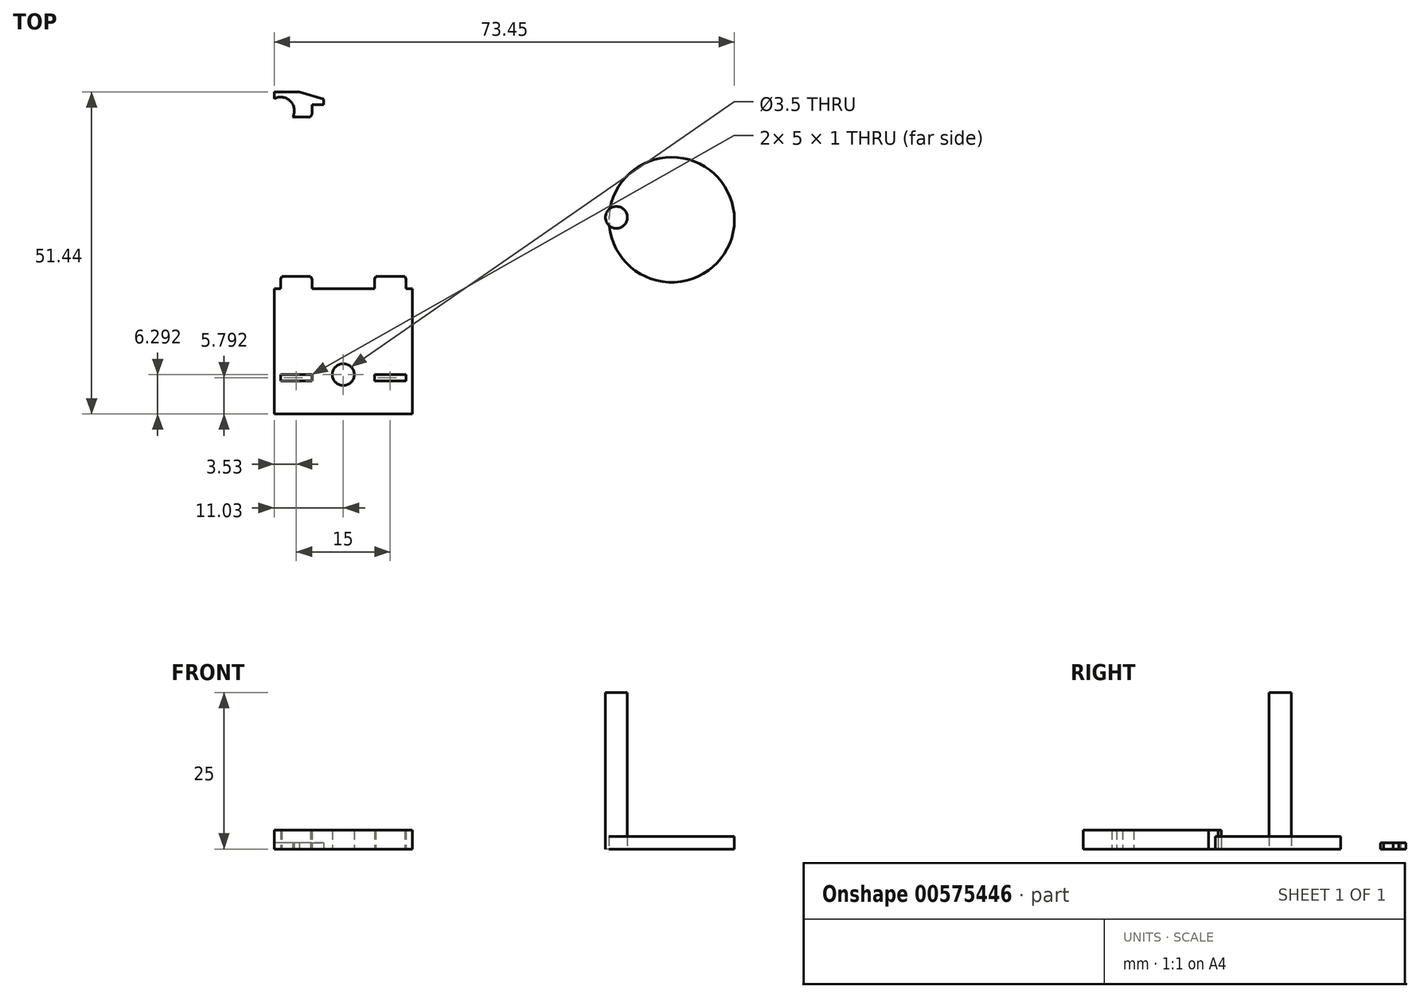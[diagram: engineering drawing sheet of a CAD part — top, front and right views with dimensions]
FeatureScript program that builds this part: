
annotation { "Feature Type Name" : "Feature", "Feature Type Description" : "" }
export const myFeature = defineFeature(function(context is Context, id is Id, definition is map)
    precondition{}
    {
        {
            assignVariable(context, id + "F0", {"name" : "blechdicke", "anyValue" : 1});
        }
        {
            assignVariable(context, id + "F1", {"name" : "kopfhoehe", "anyValue" : 2});
        }
        {
            var Q0;
            Q0=qCreatedBy(makeId("Top.planeOp"),FACE);
            var sketch = newSketch(context, id + "F2", { "sketchPlane" : qUnion([Q0])});
            skLineSegment(sketch, "E0", {"start": v(0, 0) * mm, "end": v(0, 9) * mm, "construction": true});
            skLineSegment(sketch, "E1.MirrorCS", {"start": v(-11.03, 4) * mm, "end": v(-11.03, 24) * mm});
            skLineSegment(sketch, "E2", {"start": v(-4, -10.72) * mm, "end": v(4, -10.72) * mm, "construction": true});
            skCircle(sketch, "E3", {"center": v(0, -39.15) * mm, "radius": 1.75 * mm});
            skCircle(sketch, "E4", {"center": v(52.42, -14.41) * mm, "radius": 10 * mm});
            skCircle(sketch, "E5", {"center": v(43.6, -14.03) * mm, "radius": 1.75 * mm});
            skLineSegment(sketch, "E6", {"start": v(-5, 4) * mm, "end": v(-5, 0) * mm});
            skLineSegment(sketch, "E7", {"start": v(-10, 4) * mm, "end": v(-10, 5) * mm});
            skLineSegment(sketch, "E8", {"start": v(-10, 4) * mm, "end": v(-11.03, 4) * mm});
            skLineSegment(sketch, "E9", {"start": v(0, 2) * mm, "end": v(0, 0) * mm, "construction": true});
            skLineSegment(sketch, "E10", {"start": v(-5, 4) * mm, "end": v(0, 4) * mm});
            skLineSegment(sketch, "E11", {"start": v(0, 9) * mm, "end": v(0, 17.71) * mm, "construction": true});
            skLineSegment(sketch, "E12", {"start": v(0, 17.71) * mm, "end": v(-5, 17.71) * mm, "construction": true});
            skLineSegment(sketch, "E13", {"start": v(-5, 17.71) * mm, "end": v(-10, 17.71) * mm, "construction": true});
            skLineSegment(sketch, "E14", {"start": v(-10, 17.71) * mm, "end": v(-11.03, 17.71) * mm, "construction": true});
            skLineSegment(sketch, "E15", {"start": v(-10, 17.71) * mm, "end": v(-10, 18.71) * mm});
            skLineSegment(sketch, "E16", {"start": v(-10, 18.71) * mm, "end": v(-5, 18.71) * mm});
            skLineSegment(sketch, "E17", {"start": v(-5, 18.71) * mm, "end": v(-5, 17.71) * mm});
            skLineSegment(sketch, "E18", {"start": v(-10, 17.71) * mm, "end": v(-5, 17.71) * mm});
            skLineSegment(sketch, "E19", {"start": v(-5, 2.5) * mm, "end": v(-5, 0) * mm});
            skLineSegment(sketch, "E20", {"start": v(-5.2, 2) * mm, "end": v(-9.8, 2) * mm});
            skLineSegment(sketch, "E21", {"start": v(-10, 2.5) * mm, "end": v(-10, 5) * mm});
            skLineSegment(sketch, "E22", {"start": v(-11.03, 24) * mm, "end": v(0, 24) * mm});
            skLineSegment(sketch, "E23", {"start": v(0, 9) * mm, "end": v(3, 9) * mm});
            skLineSegment(sketch, "E24", {"start": v(3, 9) * mm, "end": v(3, 6) * mm});
            skLineSegment(sketch, "E25", {"start": v(3, 6) * mm, "end": v(-17, 6) * mm});
            skLineSegment(sketch, "E26", {"start": v(-17, 6) * mm, "end": v(-3, 9) * mm});
            skLineSegment(sketch, "E27", {"start": v(-3, 9) * mm, "end": v(0, 9) * mm});
            skPoint(sketch, "E28.visualSharp", {"position": v(-5, 2) * mm});
            skLineSegment(sketch, "E29", {"start": v(-5, 2.5) * mm, "end": v(-10, 2.5) * mm, "construction": true});
            skLineSegment(sketch, "E30", {"start": v(-7.5, 2.5) * mm, "end": v(-7.5, 2) * mm, "construction": true});
            skLineSegment(sketch, "E31", {"start": v(-5, 2.5) * mm, "end": v(-5.2, 2) * mm});
            skPoint(sketch, "E32.visualSharp", {"position": v(-10, 2) * mm});
            skLineSegment(sketch, "E33", {"start": v(-10, 2.5) * mm, "end": v(-9.8, 2) * mm});
            skLineSegment(sketch, "E34.MirrorCS", {"start": v(5, 4) * mm, "end": v(0, 4) * mm});
            skLineSegment(sketch, "E35.MirrorCS", {"start": v(0, 17.71) * mm, "end": v(5, 17.71) * mm, "construction": true});
            skLineSegment(sketch, "E36.MirrorCS", {"start": v(11.03, 24) * mm, "end": v(0, 24) * mm});
            skLineSegment(sketch, "E37.MirrorCS", {"start": v(5, 2.5) * mm, "end": v(5.2, 2) * mm});
            skLineSegment(sketch, "E38.MirrorCS", {"start": v(10, 2.5) * mm, "end": v(9.8, 2) * mm});
            skLineSegment(sketch, "E39.MirrorCS", {"start": v(7.5, 2.5) * mm, "end": v(7.5, 2) * mm, "construction": true});
            skLineSegment(sketch, "E40.MirrorCS", {"start": v(5, 2.5) * mm, "end": v(10, 2.5) * mm, "construction": true});
            skLineSegment(sketch, "E41.MirrorCS", {"start": v(10, 17.71) * mm, "end": v(5, 17.71) * mm});
            skLineSegment(sketch, "E42.MirrorCS", {"start": v(5.2, 2) * mm, "end": v(9.8, 2) * mm});
            skLineSegment(sketch, "E43.MirrorCS", {"start": v(5, 2.5) * mm, "end": v(5, 0) * mm});
            skPoint(sketch, "E44.MirrorP", {"position": v(10, 2) * mm});
            skLineSegment(sketch, "E45.MirrorCS", {"start": v(10, 18.71) * mm, "end": v(5, 18.71) * mm});
            skLineSegment(sketch, "E46.MirrorCS", {"start": v(10, 4) * mm, "end": v(11.03, 4) * mm});
            skLineSegment(sketch, "E47.MirrorCS", {"start": v(10, 2.5) * mm, "end": v(10, 5) * mm});
            skLineSegment(sketch, "E48.MirrorCS", {"start": v(10, 17.71) * mm, "end": v(11.03, 17.71) * mm, "construction": true});
            skLineSegment(sketch, "E49.MirrorCS", {"start": v(5, 17.71) * mm, "end": v(10, 17.71) * mm, "construction": true});
            skLineSegment(sketch, "E50.MirrorCS", {"start": v(10, 17.71) * mm, "end": v(10, 18.71) * mm});
            skLineSegment(sketch, "E51.MirrorCS", {"start": v(11.03, 4) * mm, "end": v(11.03, 24) * mm});
            skLineSegment(sketch, "E52.MirrorCS", {"start": v(5, 4) * mm, "end": v(5, 0) * mm});
            skPoint(sketch, "E53.MirrorP", {"position": v(5, 2) * mm});
            skLineSegment(sketch, "E54.MirrorCS", {"start": v(5, 18.71) * mm, "end": v(5, 17.71) * mm});
            skLineSegment(sketch, "E55.MirrorCS", {"start": v(10, 4) * mm, "end": v(10, 5) * mm});
            skLineSegment(sketch, "E56.MirrorCS", {"start": v(0, -30.44) * mm, "end": v(0, -39.15) * mm, "construction": true});
            skLineSegment(sketch, "E57.MirrorCS", {"start": v(-5, -23.94) * mm, "end": v(-5.2, -23.44) * mm});
            skLineSegment(sketch, "E58.MirrorCS", {"start": v(5, -23.94) * mm, "end": v(5.2, -23.44) * mm});
            skLineSegment(sketch, "E59.MirrorCS", {"start": v(10, -23.94) * mm, "end": v(9.8, -23.44) * mm});
            skLineSegment(sketch, "E60.MirrorCS", {"start": v(-10, -23.94) * mm, "end": v(-9.8, -23.44) * mm});
            skLineSegment(sketch, "E61.MirrorCS", {"start": v(7.5, -23.94) * mm, "end": v(7.5, -23.44) * mm, "construction": true});
            skLineSegment(sketch, "E62.MirrorCS", {"start": v(5, -23.94) * mm, "end": v(10, -23.94) * mm, "construction": true});
            skLineSegment(sketch, "E63.MirrorCS", {"start": v(-5, -23.94) * mm, "end": v(-10, -23.94) * mm, "construction": true});
            skLineSegment(sketch, "E64.MirrorCS", {"start": v(10, -39.15) * mm, "end": v(5, -39.15) * mm});
            skLineSegment(sketch, "E65.MirrorCS", {"start": v(5.2, -23.44) * mm, "end": v(9.8, -23.44) * mm});
            skLineSegment(sketch, "E66.MirrorCS", {"start": v(-7.5, -23.94) * mm, "end": v(-7.5, -23.44) * mm, "construction": true});
            skLineSegment(sketch, "E67.MirrorCS", {"start": v(-5.2, -23.44) * mm, "end": v(-9.8, -23.44) * mm});
            skLineSegment(sketch, "E68.MirrorCS", {"start": v(-10, -39.15) * mm, "end": v(-5, -39.15) * mm});
            skLineSegment(sketch, "E69.MirrorCS", {"start": v(0, -23.44) * mm, "end": v(0, -21.44) * mm, "construction": true});
            skLineSegment(sketch, "E70.MirrorCS", {"start": v(-10, -40.15) * mm, "end": v(-5, -40.15) * mm});
            skPoint(sketch, "E71.MirrorP", {"position": v(-5, -23.44) * mm});
            skLineSegment(sketch, "E72.MirrorCS", {"start": v(-11.03, -25.44) * mm, "end": v(-11.03, -45.44) * mm});
            skLineSegment(sketch, "E73.MirrorCS", {"start": v(-5, -23.94) * mm, "end": v(-5, -21.44) * mm});
            skLineSegment(sketch, "E74.MirrorCS", {"start": v(5, -40.15) * mm, "end": v(5, -39.15) * mm});
            skPoint(sketch, "E75.MirrorP", {"position": v(5, -23.44) * mm});
            skLineSegment(sketch, "E76.MirrorCS", {"start": v(11.03, -45.44) * mm, "end": v(0, -45.44) * mm});
            skLineSegment(sketch, "E77.MirrorCS", {"start": v(0, -39.15) * mm, "end": v(5, -39.15) * mm, "construction": true});
            skLineSegment(sketch, "E78.MirrorCS", {"start": v(10, -25.44) * mm, "end": v(10, -26.44) * mm});
            skLineSegment(sketch, "E79.MirrorCS", {"start": v(5, -39.15) * mm, "end": v(10, -39.15) * mm, "construction": true});
            skPoint(sketch, "E80.MirrorP", {"position": v(10, -23.44) * mm});
            skLineSegment(sketch, "E81.MirrorCS", {"start": v(5, -25.44) * mm, "end": v(5, -21.44) * mm});
            skLineSegment(sketch, "E82.MirrorCS", {"start": v(-10, -25.44) * mm, "end": v(-11.03, -25.44) * mm});
            skLineSegment(sketch, "E83.MirrorCS", {"start": v(5, -25.44) * mm, "end": v(0, -25.44) * mm});
            skLineSegment(sketch, "E84.MirrorCS", {"start": v(-10, -39.15) * mm, "end": v(-11.03, -39.15) * mm, "construction": true});
            skLineSegment(sketch, "E85.MirrorCS", {"start": v(-5, -40.15) * mm, "end": v(-5, -39.15) * mm});
            skLineSegment(sketch, "E86.MirrorCS", {"start": v(10, -23.94) * mm, "end": v(10, -26.44) * mm});
            skLineSegment(sketch, "E87.MirrorCS", {"start": v(-11.03, -45.44) * mm, "end": v(0, -45.44) * mm});
            skLineSegment(sketch, "E88.MirrorCS", {"start": v(-5, -39.15) * mm, "end": v(-10, -39.15) * mm, "construction": true});
            skLineSegment(sketch, "E89.MirrorCS", {"start": v(-10, -23.94) * mm, "end": v(-10, -26.44) * mm});
            skLineSegment(sketch, "E90.MirrorCS", {"start": v(10, -39.15) * mm, "end": v(10, -40.15) * mm});
            skLineSegment(sketch, "E91.MirrorCS", {"start": v(-10, -39.15) * mm, "end": v(-10, -40.15) * mm});
            skLineSegment(sketch, "E92.MirrorCS", {"start": v(5, -23.94) * mm, "end": v(5, -21.44) * mm});
            skLineSegment(sketch, "E93.MirrorCS", {"start": v(-10, -25.44) * mm, "end": v(-10, -26.44) * mm});
            skLineSegment(sketch, "E94.MirrorCS", {"start": v(-5, -25.44) * mm, "end": v(0, -25.44) * mm});
            skPoint(sketch, "E95.MirrorP", {"position": v(-10, -23.44) * mm});
            skLineSegment(sketch, "E96.MirrorCS", {"start": v(10, -39.15) * mm, "end": v(11.03, -39.15) * mm, "construction": true});
            skLineSegment(sketch, "E97.MirrorCS", {"start": v(-5, -25.44) * mm, "end": v(-5, -21.44) * mm});
            skLineSegment(sketch, "E98.MirrorCS", {"start": v(10, -40.15) * mm, "end": v(5, -40.15) * mm});
            skLineSegment(sketch, "E99.MirrorCS", {"start": v(0, -39.15) * mm, "end": v(-5, -39.15) * mm, "construction": true});
            skLineSegment(sketch, "E100.MirrorCS", {"start": v(0, -21.44) * mm, "end": v(0, -30.44) * mm, "construction": true});
            skLineSegment(sketch, "E101.MirrorCS", {"start": v(11.03, -25.44) * mm, "end": v(11.03, -45.44) * mm});
            skLineSegment(sketch, "E102.MirrorCS", {"start": v(10, -25.44) * mm, "end": v(11.03, -25.44) * mm});
            skLineSegment(sketch, "E103", {"start": v(-3.12, 6) * mm, "end": v(-3.12, 4) * mm});
            skLineSegment(sketch, "E104", {"start": v(-3.12, 4) * mm, "end": v(0, 4) * mm});
            skLineSegment(sketch, "E105", {"start": v(0, 4) * mm, "end": v(-7, 6) * mm});
            skLineSegment(sketch, "E106", {"start": v(-3.12, 6) * mm, "end": v(-7, 6) * mm});
            skLineSegment(sketch, "E107.MirrorCS", {"start": v(3.12, 6) * mm, "end": v(7, 6) * mm});
            skLineSegment(sketch, "E108.MirrorCS", {"start": v(3.12, 6) * mm, "end": v(3.12, 4) * mm});
            skLineSegment(sketch, "E109.MirrorCS", {"start": v(3.12, 4) * mm, "end": v(0, 4) * mm});
            skLineSegment(sketch, "E110", {"start": v(-1.5, 9) * mm, "end": v(0, 13.36) * mm});
            skLineSegment(sketch, "E111.MirrorCS", {"start": v(1.5, 9) * mm, "end": v(0, 13.36) * mm});
            skCircle(sketch, "E112", {"center": v(-10, 3.3) * mm, "radius": 0.16 * mm});
            skCircle(sketch, "E113", {"center": v(-10, 2.89) * mm, "radius": 0.11 * mm});
            skCircle(sketch, "E114", {"center": v(-10, 3) * mm, "radius": 2.2 * mm});
            skSolve(sketch);
        }
        {
            var Q0;
            Q0=makeQuery(id+"F2.imprint","IMPRINT",FACE,{"disambiguationData":[TD([[makeQuery(id+"F2.imprint","IMPRINT",EDGE,{"derivedFrom":sQuery(id+"F2.wireOp",EDGE,"E1.MirrorCS")}),-1.0]])]});
            extrude(context, id + "F3", {"entities" : qUnion([Q0]), "depth" : (getVariable(context, 'blechdicke')) * mm, "offsetDistance" : 25 * mm});
        }
        {
            var Q0;
            Q0=makeQuery(id+"F2.imprint","IMPRINT",FACE,{"disambiguationData":[TD([[makeQuery(id+"F2.imprint","IMPRINT",EDGE,{"derivedFrom":sQuery(id+"F2.wireOp",EDGE,"E3")}),-1.0]])]});
            extrude(context, id + "F4", {"entities" : qUnion([Q0]), "depth" : 3 * mm, "offsetDistance" : 25 * mm});
        }
        {
            var Q0;
            Q0=makeQuery(id+"F2.imprint","IMPRINT",FACE,{"disambiguationData":[TD([[makeQuery(id+"F2.imprint","IMPRINT",EDGE,{"derivedFrom":sQuery(id+"F2.wireOp",EDGE,"E4")}),1.0]])]});
            extrude(context, id + "F5", {"entities" : qUnion([Q0]), "depth" : (getVariable(context, 'kopfhoehe')) * mm, "offsetDistance" : 25 * mm});
        }
        {
            var Q0;
            Q0=makeQuery(id+"F2.imprint","IMPRINT",FACE,{"disambiguationData":[TD([[makeQuery(id+"F2.imprint","IMPRINT",EDGE,{"derivedFrom":sQuery(id+"F2.wireOp",EDGE,"E5")}),1.0]])]});
            extrude(context, id + "F6", {"entities" : qUnion([Q0]), "depth" : 25 * mm, "offsetDistance" : 25 * mm});
        }
    });
